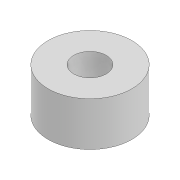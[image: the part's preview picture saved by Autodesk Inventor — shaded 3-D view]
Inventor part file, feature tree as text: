
AUTODESK INVENTOR PART (.ipt)
format: ipt  version: 2022 (Build 260153000, 153)  size: 84,480 bytes
history: native  units: mm
features: extrude x1, sketch x1
ambient origin geometry x8: Origin, YZ Plane, XZ Plane, XY Plane, X Axis, Y Axis, Z Axis, Center Point
bodies: Solid1 (feature_tree)
feature tree (2):
  extrude  "Extrusion1"  Depth=4.2mm
  sketch  "Sketch1"  dims[d0=3.1mm d1=8.0mm d2=4.2mm d3=0.0mm]
